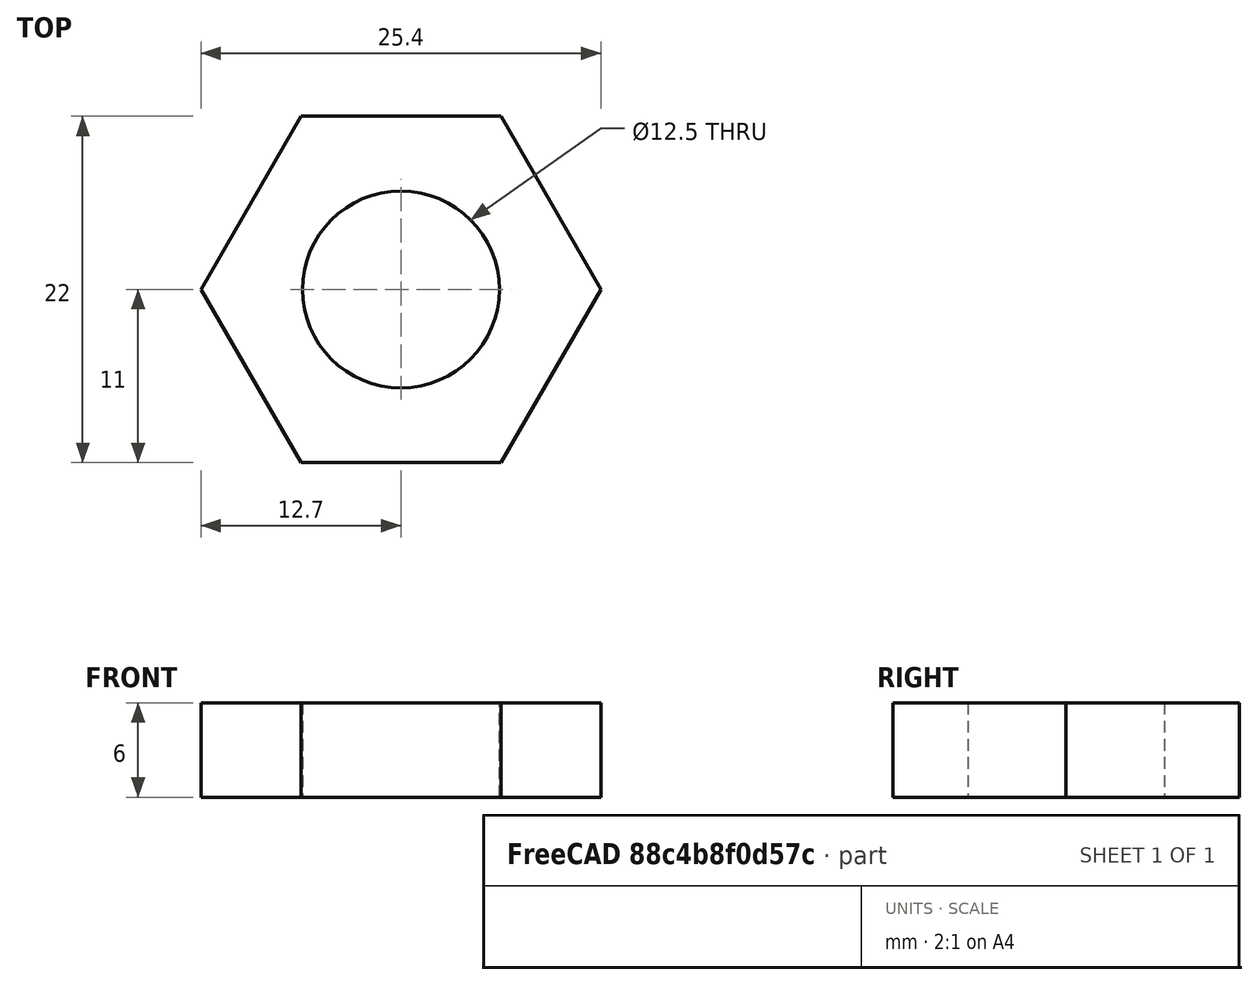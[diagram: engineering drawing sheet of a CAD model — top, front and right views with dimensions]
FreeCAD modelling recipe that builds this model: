
FCSTD DOCUMENT  (FreeCAD 0.19R24267 +99 (Git))
Label: Flexible coolant pipe nut
License: All rights reserved
LicenseURL: http://en.wikipedia.org/wiki/All_rights_reserved
objects: Sketcher::SketchObject×1, PartDesign::Pad×1, PartDesign::Body×1
note: 4 computed .brp shape members not serialized (recipe doc carries the construction recipe); baked Part::Feature solids carry a one-line shape summary decoded from their .brp

FEATURE [Sketcher::SketchObject] Sketch
  FullyConstrained = true
  MapMode = 5
  Support = -> [XY_Plane]
  sketch-geometry (8):
    g0: Circle CenterX=0 CenterY=0 CenterZ=0 NormalX=0 NormalY=0 NormalZ=1 AngleXU=0 Radius=6.25
    g1: LineSegment StartX=12.7017 StartY=0 StartZ=0 EndX=6.35085 EndY=11 EndZ=0
    g2: LineSegment StartX=6.35085 StartY=11 StartZ=0 EndX=-6.35085 EndY=11 EndZ=0
    g3: LineSegment StartX=-6.35085 StartY=11 StartZ=0 EndX=-12.7017 EndY=-1.7746e-12 EndZ=0
    g4: LineSegment StartX=-12.7017 StartY=-1.7746e-12 StartZ=0 EndX=-6.35085 EndY=-11 EndZ=0
    g5: LineSegment StartX=-6.35085 StartY=-11 StartZ=0 EndX=6.35085 EndY=-11 EndZ=0
    g6: LineSegment StartX=6.35085 StartY=-11 StartZ=0 EndX=12.7017 EndY=0 EndZ=0
    g7: Circle CenterX=0 CenterY=0 CenterZ=0 NormalX=0 NormalY=0 NormalZ=1 AngleXU=0 Radius=12.7017
  constraints (18):
    c: Coincident(g0,g-1)
    c: Coincident(g1,g2)
    c: Coincident(g2,g3)
    c: Coincident(g3,g4)
    c: Coincident(g4,g5)
    c: Coincident(g5,g6)
    c: Coincident(g6,g1)
    c: Equal(g1, g2-g6) x5
    c: PointOnObject(g1,g7)
    c: PointOnObject(g2,g7)
    c: PointOnObject(g3,g7)
    c: PointOnObject(g4,g7)
    c: PointOnObject(g5,g7)
    c: PointOnObject(g6,g7)
    c: Coincident(g7,g0)
    c: PointOnObject(g6,g-1)
    c: DistanceY(g4,g2) = 22
    c: Diameter(g0) = 12.5
FEATURE [PartDesign::Pad] Pad  label="Thickness"
  Direction = (1,1,1)
  Length = 6
  Length2 = 100
  Profile = -> Sketch
  Type = 0
FEATURE [PartDesign::Body] Body
  Group = -> [Sketch,Pad]
  Origin = -> Origin
  Tip = -> Pad
